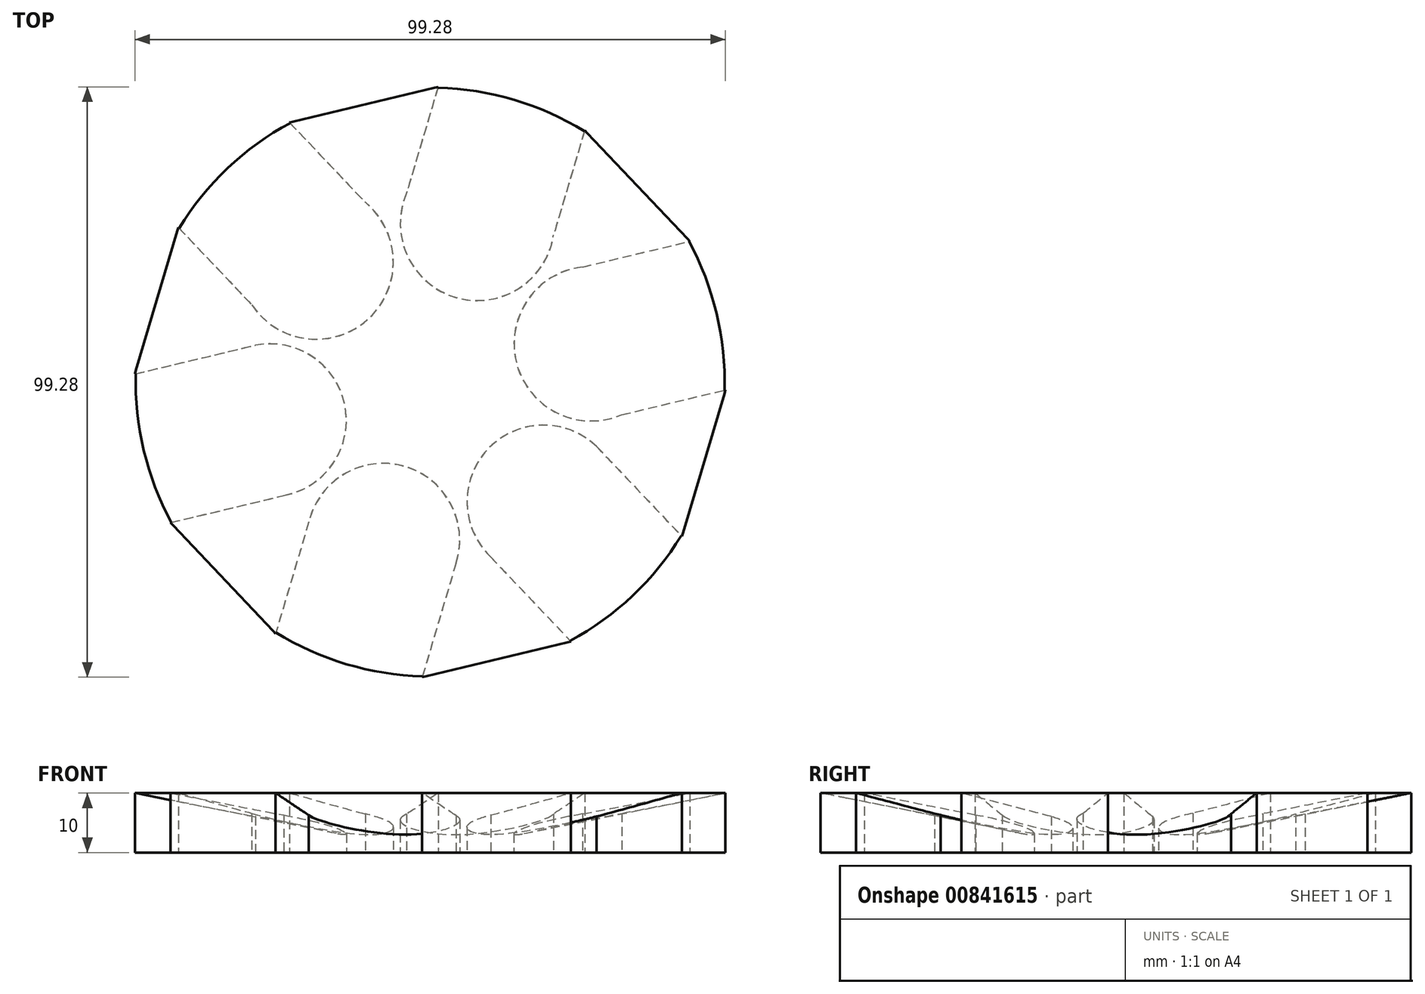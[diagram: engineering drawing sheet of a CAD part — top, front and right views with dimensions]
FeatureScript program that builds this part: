
annotation { "Feature Type Name" : "Feature", "Feature Type Description" : "" }
export const myFeature = defineFeature(function(context is Context, id is Id, definition is map)
    precondition{}
    {
        {
            var Q0;
            Q0=qCreatedBy(makeId("Top.planeOp"),FACE);
            var sketch = newSketch(context, id + "F0", { "sketchPlane" : qUnion([Q0])});
            skLineSegment(sketch, "E0.0", {"start": v(-42.32, 25.98) * mm, "end": v(-23.66, 43.66) * mm});
            skLineSegment(sketch, "E0.1", {"start": v(-23.66, 43.66) * mm, "end": v(1.34, 49.64) * mm});
            skLineSegment(sketch, "E0.2", {"start": v(1.34, 49.64) * mm, "end": v(25.98, 42.32) * mm});
            skLineSegment(sketch, "E0.3", {"start": v(25.98, 42.32) * mm, "end": v(43.66, 23.66) * mm});
            skLineSegment(sketch, "E0.4", {"start": v(43.66, 23.66) * mm, "end": v(49.64, -1.34) * mm});
            skLineSegment(sketch, "E0.5", {"start": v(49.64, -1.34) * mm, "end": v(42.32, -25.98) * mm});
            skLineSegment(sketch, "E0.6", {"start": v(42.32, -25.98) * mm, "end": v(23.66, -43.66) * mm});
            skLineSegment(sketch, "E0.7", {"start": v(23.66, -43.66) * mm, "end": v(-1.34, -49.64) * mm});
            skLineSegment(sketch, "E0.8", {"start": v(-1.34, -49.64) * mm, "end": v(-25.98, -42.32) * mm});
            skLineSegment(sketch, "E0.9", {"start": v(-25.98, -42.32) * mm, "end": v(-43.66, -23.66) * mm});
            skLineSegment(sketch, "E0.10", {"start": v(-43.66, -23.66) * mm, "end": v(-49.64, 1.34) * mm});
            skLineSegment(sketch, "E0.11", {"start": v(-49.64, 1.34) * mm, "end": v(-42.32, 25.98) * mm});
            skPoint(sketch, "E0.0.midPoint", {"position": v(-32.99, 34.82) * mm});
            skLineSegment(sketch, "E1", {"start": v(-42.32, 25.98) * mm, "end": v(-26.96, 9.77) * mm});
            skLineSegment(sketch, "E2", {"start": v(-23.66, 43.66) * mm, "end": v(-8.7, 27.88) * mm});
            skLineSegment(sketch, "E3", {"start": v(1.34, 49.64) * mm, "end": v(-4.85, 28.8) * mm});
            skLineSegment(sketch, "E4", {"start": v(25.98, 42.32) * mm, "end": v(19.73, 21.27) * mm});
            skLineSegment(sketch, "E5", {"start": v(-49.64, 1.34) * mm, "end": v(-29.38, 6.19) * mm});
            skLineSegment(sketch, "E6", {"start": v(-43.66, -23.66) * mm, "end": v(-23.28, -18.78) * mm});
            skPoint(sketch, "E7", {"position": v(-24.64, 7.32) * mm});
            skPoint(sketch, "E8", {"position": v(-5.98, 25) * mm});
            skPoint(sketch, "E9", {"position": v(18.66, 17.68) * mm});
            skPoint(sketch, "E10", {"position": v(24.64, -7.32) * mm});
            skPoint(sketch, "E11", {"position": v(5.98, -25) * mm});
            skPoint(sketch, "E12", {"position": v(-18.66, -17.68) * mm});
            skPoint(sketch, "E13.center.orphan", {"position": v(-21.65, -5.18) * mm});
            skPoint(sketch, "E14", {"position": v(-14.43, -3.45) * mm});
            skArc(sketch, "E15", {"start": v(-24.63, -19.1) * mm, "mid": v(-14.3, -4.08) * mm, "end": v(-29.38, 6.19) * mm});
            skPoint(sketch, "E16", {"position": v(-10.2, 10.77) * mm});
            skPoint(sketch, "E17", {"position": v(4.23, 14.23) * mm});
            skPoint(sketch, "E18", {"position": v(14.43, 3.45) * mm});
            skPoint(sketch, "E19", {"position": v(10.2, -10.77) * mm});
            skPoint(sketch, "E20", {"position": v(-4.23, -14.23) * mm});
            skArc(sketch, "E21", {"start": v(-30, 12.97) * mm, "mid": v(-10.46, 10.54) * mm, "end": v(-10.92, 30.22) * mm});
            skArc(sketch, "E22.MirrorCS", {"start": v(32.21, -5.51) * mm, "mid": v(14.52, 3.12) * mm, "end": v(25.65, 19.35) * mm});
            skArc(sketch, "E23.MirrorCS", {"start": v(10.2, -29.46) * mm, "mid": v(9.75, -11.22) * mm, "end": v(28, -10.86) * mm});
            skArc(sketch, "E24", {"start": v(-3.95, 31.82) * mm, "mid": v(4.35, 14.19) * mm, "end": v(20.75, 24.71) * mm});
            skArc(sketch, "E25", {"start": v(4.36, -30.45) * mm, "mid": v(-4.45, -14.16) * mm, "end": v(-20.4, -23.55) * mm});
            skLineSegment(sketch, "E26.trimOffspring", {"start": v(22.52, 18.6) * mm, "end": v(43.66, 23.66) * mm});
            skLineSegment(sketch, "E27.trimOffspring", {"start": v(-20.02, -22.24) * mm, "end": v(-25.98, -42.32) * mm});
            skPoint(sketch, "E28.orphan", {"position": v(13.66, 45.98) * mm});
            skPoint(sketch, "E29.orphan", {"position": v(46.65, 11.16) * mm});
            skPoint(sketch, "E30.orphan", {"position": v(32.99, -34.82) * mm});
            skPoint(sketch, "E31.trimOffspring.end.orphan", {"position": v(-13.66, -45.98) * mm});
            skPoint(sketch, "E32.start.orphan", {"position": v(-46.65, -11.16) * mm});
            skLineSegment(sketch, "E33.trimOffspring", {"start": v(27.92, -6.54) * mm, "end": v(49.64, -1.34) * mm});
            skLineSegment(sketch, "E34.trimOffspring", {"start": v(28, -10.86) * mm, "end": v(42.32, -25.98) * mm});
            skLineSegment(sketch, "E35.trimOffspring", {"start": v(4.5, -29.98) * mm, "end": v(-1.34, -49.64) * mm});
            skLineSegment(sketch, "E36.trimOffspring", {"start": v(9.25, -28.45) * mm, "end": v(23.66, -43.66) * mm});
            skSolve(sketch);
        }
        {
            var Q0;
            {var subQ32=sQuery(id+"F0.wireOp",EDGE,"E0.1");Q0=makeQuery(id+"F0.imprint","IMPRINT",FACE,{"disambiguationData":[TD([[makeQuery(id+"F0.imprint","IMPRINT",EDGE,{"derivedFrom":subQ32}),-1.0]])]});}
            extrude(context, id + "F1", {"entities" : qUnion([Q0]), "depth" : 10 * mm, "offsetDistance" : 25 * mm});
        }
        {
            var Q0;
            Q0=qCreatedBy(makeId("Front.planeOp"),FACE);
            var sketch = newSketch(context, id + "F2", { "sketchPlane" : qUnion([Q0])});
            skLineSegment(sketch, "E37", {"start": v(0, 0) * mm, "end": v(49.5, 10) * mm});
            skLineSegment(sketch, "E38", {"start": v(49.5, 10) * mm, "end": v(0, 10) * mm});
            skLineSegment(sketch, "E39", {"start": v(0, 10) * mm, "end": v(0, 0) * mm});
            skSolve(sketch);
        }
        {
            var Q0;
            Q0 = qSketchRegion(id + "F2", true);
            var Q1;
            Q1=sQuery(id+"F2.wireOp",EDGE,"E39");
            revolve(context, id + "F3", {"operationType" : NewBodyOperationType.ADD, "surfaceOperationType" : NewSurfaceOperationType.NEW, "entities" : qUnion([Q0]), "axis" : qUnion([Q1]), "revolveType" : RevolveType.FULL});
        }
    });
